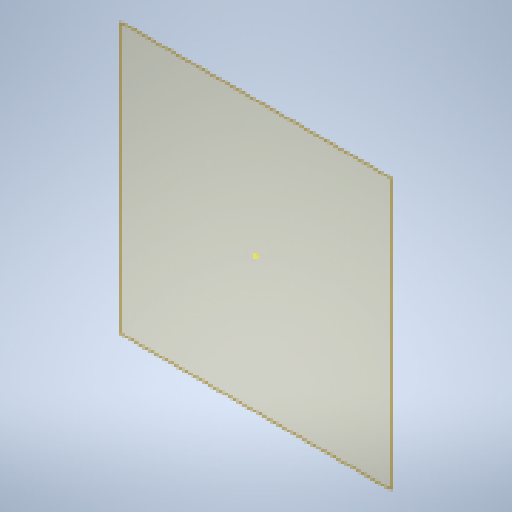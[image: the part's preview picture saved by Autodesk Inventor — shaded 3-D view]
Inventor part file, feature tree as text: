
AUTODESK INVENTOR PART (.ipt)
format: ipt  version: 2023.1 (Build 271208000, 208)  size: 184,320 bytes
history: native  units: mm
features: other x4, sketch x2, extrude x2, plane x1
ambient origin geometry x8: Origin, YZ Plane, XZ Plane, XY Plane, X Axis, Y Axis, Z Axis, Center Point
bodies: Solid1 (feature_tree)
feature tree (9):
  other  "<userpath>\Documents\WaterPump\Parameters.xlsx"
  plane  "Work Plane1"
  sketch  "Sketch1"  dims[d0=21.0mm d1=15.5mm]
  extrude  "Extrusion1"  Depth=21.0mm
  extrude  "Extrusion2"  Depth=5.5mm
  sketch  "Sketch2"  dims[d2=31.0mm d3=4.363323mm d4=16.875mm d5=18.25mm d6=19.625mm d7=20.0mm d8=20.0mm d9=2.0mm d10=2.0mm d11=2.0mm d12=2.0mm d13=2.0mm d14=18.0mm d15=0.0mm d16=2.0mm d17=3.0mm d18=0.0mm d19=5.5mm]
  other  "<userpath>\Documents\WaterPump\Assembly1.iam"
  other  "Assembly1.iam"
  other  "Motor:1"
